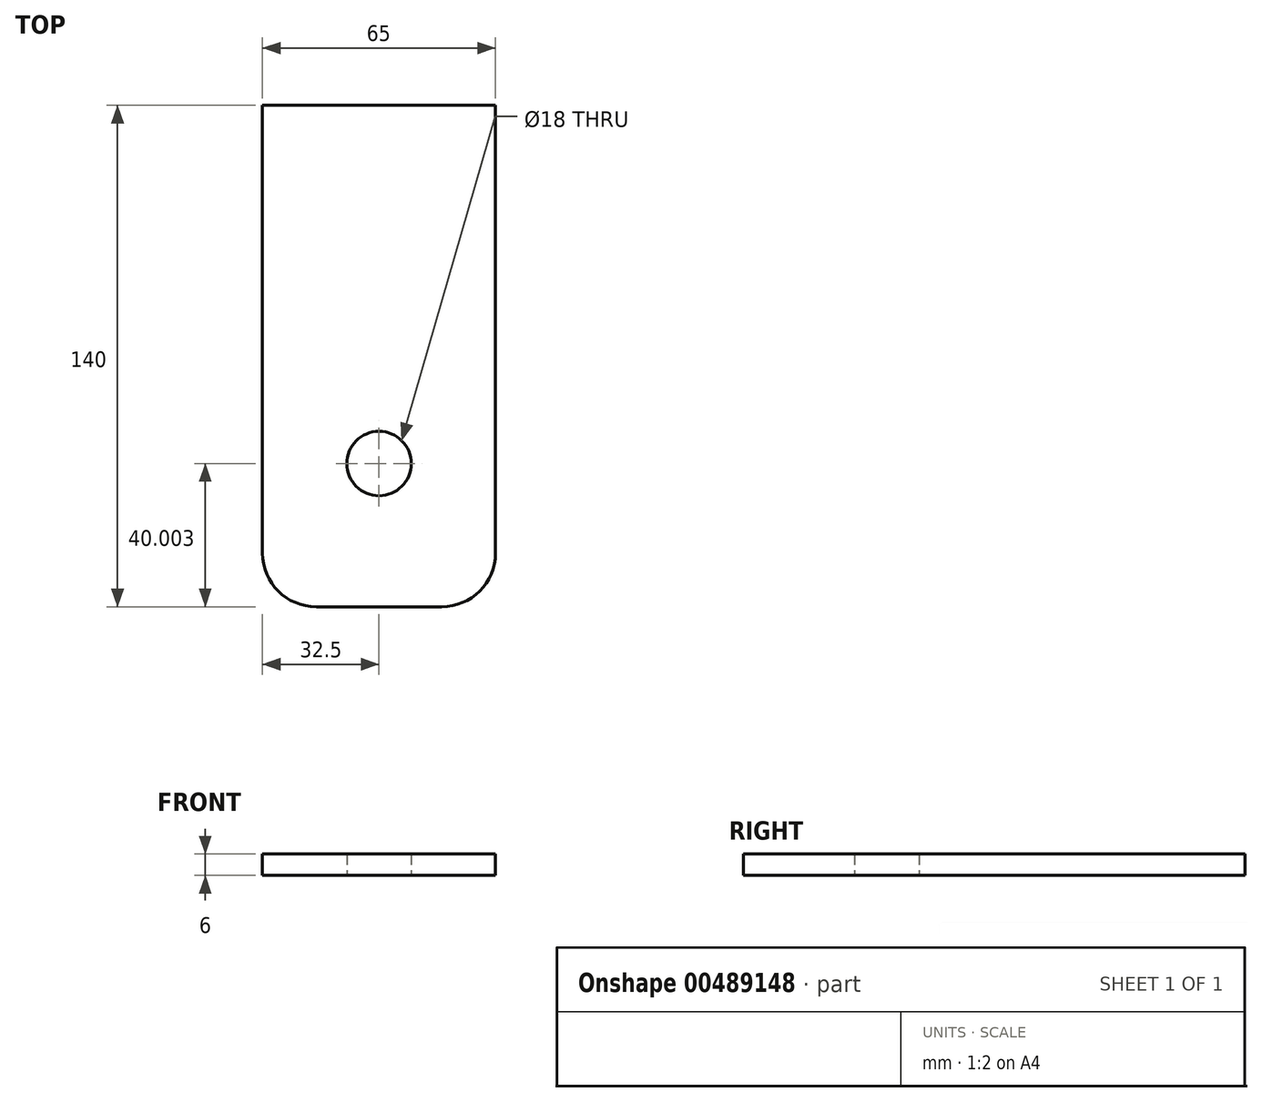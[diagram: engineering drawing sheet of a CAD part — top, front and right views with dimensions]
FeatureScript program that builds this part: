
annotation { "Feature Type Name" : "Feature", "Feature Type Description" : "" }
export const myFeature = defineFeature(function(context is Context, id is Id, definition is map)
    precondition{}
    {
        {
            var Q0;
            Q0=qCreatedBy(makeId("Top.planeOp"),FACE);
            var sketch = newSketch(context, id + "F0", { "sketchPlane" : qUnion([Q0])});
            skLineSegment(sketch, "E0.bottom", {"start": v(-65, 87.3) * mm, "end": v(0, 87.3) * mm});
            skLineSegment(sketch, "E0.top", {"start": v(-50, -52.7) * mm, "end": v(-15, -52.7) * mm});
            skLineSegment(sketch, "E0.left", {"start": v(-65, 87.3) * mm, "end": v(-65, -37.7) * mm});
            skLineSegment(sketch, "E0.right", {"start": v(0, 87.3) * mm, "end": v(0, -37.7) * mm});
            skPoint(sketch, "E1.visualSharp", {"position": v(-65, -52.7) * mm});
            skArc(sketch, "E1.filletArc", {"start": v(-65, -37.7) * mm, "mid": v(-60.6, -48.3) * mm, "end": v(-50, -52.7) * mm});
            skPoint(sketch, "E2.visualSharp", {"position": v(0, -52.7) * mm});
            skArc(sketch, "E2.filletArc", {"start": v(-15, -52.7) * mm, "mid": v(-4.4, -48.3) * mm, "end": v(0, -37.7) * mm});
            skCircle(sketch, "E3", {"center": v(-32.5, -12.7) * mm, "radius": 9 * mm});
            skSolve(sketch);
        }
        {
            var Q0;
            Q0=makeQuery(id+"F0.imprint","IMPRINT",FACE,{"disambiguationData":[TD([[makeQuery(id+"F0.imprint","IMPRINT",EDGE,{"derivedFrom":sQuery(id+"F0.wireOp",EDGE,"E0.bottom")}),-1.0]])]});
            extrude(context, id + "F1", {"entities" : qUnion([Q0]), "depth" : 6 * mm});
        }
    });
